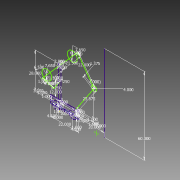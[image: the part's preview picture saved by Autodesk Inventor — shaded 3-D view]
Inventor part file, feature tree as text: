
AUTODESK INVENTOR PART (.ipt)
format: ipt  version: 2014 (Build 180170000, 170)  size: 133,632 bytes
history: native  units: in
note: dims shown in document units (in); Inventor stores cm internally (conversion verified against a paired STEP export)
features: sketch x1
ambient origin geometry x8: Origin, YZ Plane, XZ Plane, XY Plane, X Axis, Y Axis, Z Axis, Center Point
feature tree (1):
  sketch  "Sketch1"  dims[d0=22.0in d1=2.0in d2=6.0in d3=6.0in d4=4.5in d5=4.5in d6=1.0in d7=1.0in d8=1.0in d9=3.0in d10=1.5in d11=3.0in d12=1.0in d13=2.0in d14=28.0in d15=1.0in d16=14.0in d24=0.0in d26=2.0in d29=0.25in d36=0.5in d37=2.5in d44=0.5in d45=1.0in d46=1.0in d48=21.5in d49=21.5in d50=7.65in d51=7.65in d52=6.5in d53=6.5in d56=25.875in d57=4.0in d68=60.0in d70=1.375in d72=0.0in d74=0.5in d75=0.0in d117=0.5in d120=0.5in d121=1.0in d122=20.0in d146=22.0in d174=0.25in d175=12.0in d176=1.0in d177=1.0in d178=0.25in d179=9.3875in d180=8.0in]
